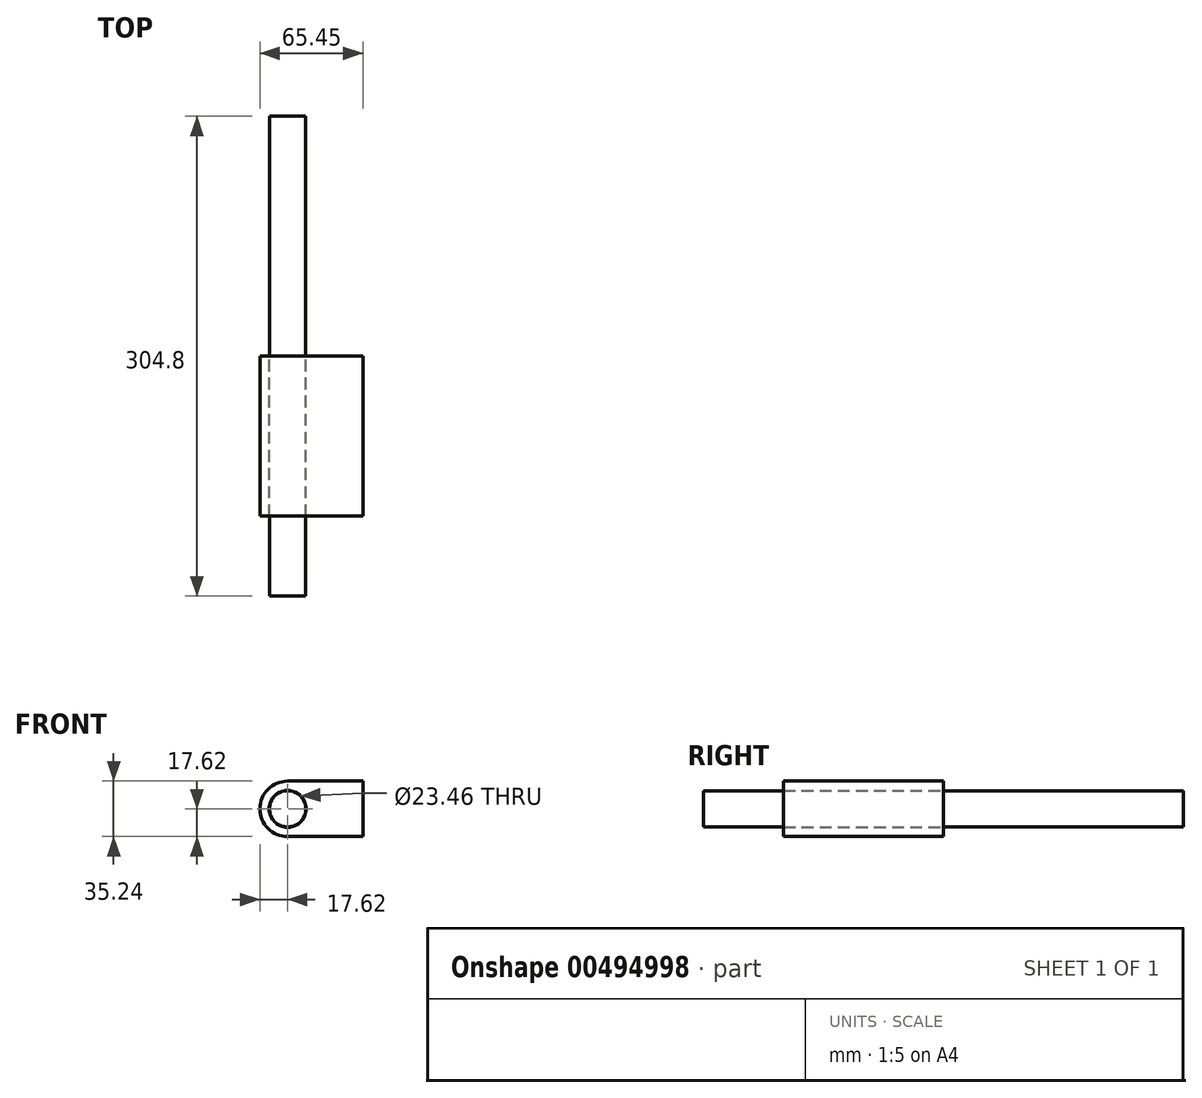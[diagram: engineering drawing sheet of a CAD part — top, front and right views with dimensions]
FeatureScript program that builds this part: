
annotation { "Feature Type Name" : "Feature", "Feature Type Description" : "" }
export const myFeature = defineFeature(function(context is Context, id is Id, definition is map)
    precondition{}
    {
        {
            var Q0;
            Q0=qCreatedBy(makeId("Front.planeOp"),FACE);
            var sketch = newSketch(context, id + "F0", { "sketchPlane" : qUnion([Q0])});
            skCircle(sketch, "E0", {"center": v(0, 0) * mm, "radius": 11.73 * mm});
            skArc(sketch, "E1", {"start": v(0, 17.62) * mm, "mid": v(-17.62, 0) * mm, "end": v(0, -17.62) * mm});
            skLineSegment(sketch, "E2", {"start": v(0, 17.62) * mm, "end": v(47.83, 17.62) * mm});
            skLineSegment(sketch, "E3", {"start": v(0, -17.62) * mm, "end": v(47.83, -17.62) * mm});
            skLineSegment(sketch, "E4", {"start": v(47.83, -17.62) * mm, "end": v(47.83, 17.62) * mm});
            skSolve(sketch);
        }
        {
            var Q0;
            Q0=makeQuery(id+"F0.imprint","IMPRINT",FACE,{"disambiguationData":[TD([[makeQuery(id+"F0.imprint","IMPRINT",EDGE,{"derivedFrom":sQuery(id+"F0.wireOp",EDGE,"E0")}),-1.0]])]});
            extrude(context, id + "F1", {"entities" : qUnion([Q0]), "depth" : 101.6 * mm});
        }
        {
            var Q0;
            Q0=makeQuery(id+"F1.opExtrude","CAP_FACE",FACE,{"disambiguationData":[OSD([sQuery(id+"F0.wireOp",EDGE,"E0"),sQuery(id+"F0.wireOp",EDGE,"E1"),sQuery(id+"F0.wireOp",EDGE,"E2"),sQuery(id+"F0.wireOp",EDGE,"E3"),sQuery(id+"F0.wireOp",EDGE,"E4")])],"isStart":false});
            var sketch = newSketch(context, id + "F2", { "sketchPlane" : qUnion([Q0])});
            skCircle(sketch, "E5", {"center": v(0, 0) * mm, "radius": 11.5 * mm});
            skSolve(sketch);
        }
        {
            var Q0;
            Q0=makeQuery(id+"F2.imprint","IMPRINT",FACE,{"disambiguationData":[TD([[makeQuery(id+"F2.imprint","IMPRINT",EDGE,{"derivedFrom":sQuery(id+"F2.wireOp",EDGE,"E5")}),1.0]])]});
            extrude(context, id + "F3", {"entities" : qUnion([Q0]), "depth" : 50.8 * mm});
        }
        {
            var Q0;
            Q0=makeQuery(id+"F3.opExtrude","CAP_FACE",FACE,{"disambiguationData":[OSD([sQuery(id+"F2.wireOp",EDGE,"E5")])],"isStart":true});
            extrude(context, id + "F4", {"entities" : qUnion([Q0]), "operationType" : NewBodyOperationType.ADD, "depth" : 254 * mm});
        }
    });
